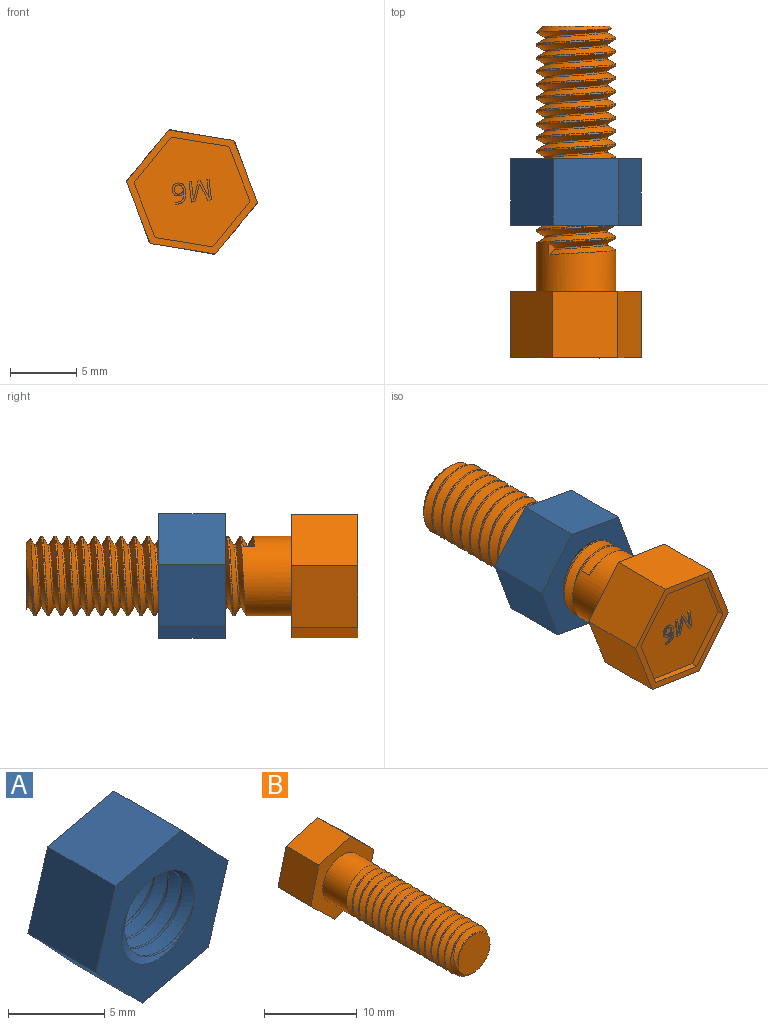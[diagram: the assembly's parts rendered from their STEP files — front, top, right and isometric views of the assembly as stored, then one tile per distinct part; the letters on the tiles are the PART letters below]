
ASSEMBLY  parts=2 mates=1
PART A: 12 faces, bbox 10.1x6.2x9.9 mm
  f0: plane 10.11x9.94mm, normal (0,-1,0), area 42.3mm2, adj f2,f3,f4,f5,f6,f7,f8,f9
  f1: plane 10.11x9.94mm, normal (0,1,0), area 42.3mm2, adj f2,f3,f4,f5,f6,f7,f8,f9
  f2: plane 5x4.78mm, normal (0.96,0,-0.29), area 25mm2, adj f0,f1,f3,f7
  f3: plane 5x3.65mm, normal (0.73,0,0.68), area 25mm2, adj f0,f1,f2,f4
  f4: plane 5x4.87mm, normal (-0.23,0,0.97), area 25mm2, adj f0,f1,f3,f5
  f5: plane 5x4.78mm, normal (-0.96,0,0.29), area 25mm2, adj f0,f1,f4,f6
  f6: plane 5x3.65mm, normal (-0.73,0,-0.68), area 25mm2, adj f0,f1,f5,f7
  f7: plane 5x4.87mm, normal (0.23,0,-0.97), area 25mm2, adj f0,f1,f2,f6
  f8: cylinder r=3mm len=6mm, axis (0,1,0), area 12.3mm2, adj f0,f1,f9,f11
  f9: bspline ~6.93x6mm, area 61.2mm2, adj f0,f1,f8,f10
  f10: cylinder r=2.37mm len=5mm, axis (0,1,0), area 11.6mm2, adj f0,f1,f9,f11
  f11: bspline ~6.93x6mm, area 61.2mm2, adj f0,f1,f8,f10
PART B: 84 faces, bbox 9.6x25.4x9.7 mm
  f0: plane 5x4.85mm, normal (0.97,0,-0.24), area 25mm2, adj f1,f5,f6,f7
  f1: plane 5x3.59mm, normal (0.7,0,0.72), area 25mm2, adj f0,f2,f6,f7
  f2: plane 5x4.81mm, normal (-0.27,0,0.96), area 25mm2, adj f1,f3,f6,f7
  f3: plane 5x4.85mm, normal (-0.97,0,0.24), area 25mm2, adj f2,f4,f6,f7
  f4: plane 5x3.59mm, normal (-0.7,0,-0.72), area 25mm2, adj f3,f5,f6,f7
  f5: plane 5x4.81mm, normal (0.27,0,-0.96), area 25mm2, adj f0,f4,f6,f7
  f6: plane 9.7x9.62mm, normal (0,-1,0), area 36.7mm2, adj f0,f1,f2,f3,f4,f5,f24
  f7: plane 9.7x9.62mm, normal (0,1,0), area 14.1mm2, adj f0,f1,f2,f3,f4,f5,f26,f27
  f8: cylinder r=3mm len=2.15mm, axis (0,1,0), area 0.1mm2, adj f9,f33,f35
  f9: cylinder r=3mm len=6mm, axis (0,1,0), area 2.4mm2, adj f8,f10,f35,f37
  f10: cylinder r=3mm len=6mm, axis (0,1,0), area 2.4mm2, adj f9,f11,f35,f37
  f11: cylinder r=3mm len=6mm, axis (0,1,0), area 2.4mm2, adj f10,f12,f35,f37
  f12: cylinder r=3mm len=6mm, axis (0,1,0), area 2.4mm2, adj f11,f13,f35,f37
  f13: cylinder r=3mm len=6mm, axis (0,1,0), area 2.4mm2, adj f12,f14,f35,f37
  f14: cylinder r=3mm len=6mm, axis (0,1,0), area 2.4mm2, adj f13,f15,f35,f37
  f15: cylinder r=3mm len=6mm, axis (0,1,0), area 2.4mm2, adj f14,f16,f35,f37
  f16: cylinder r=3mm len=6mm, axis (0,1,0), area 2.4mm2, adj f15,f17,f35,f37
  f17: cylinder r=3mm len=6mm, axis (0,1,0), area 2.4mm2, adj f16,f18,f35,f37
  f18: cylinder r=3mm len=6mm, axis (0,1,0), area 2.4mm2, adj f17,f19,f35,f37
  f19: cylinder r=3mm len=6mm, axis (0,1,0), area 2.4mm2, adj f18,f20,f35,f37
  f20: cylinder r=3mm len=6mm, axis (0,1,0), area 2.4mm2, adj f19,f21,f35,f37
  f21: cylinder r=3mm len=6mm, axis (0,1,0), area 2.4mm2, adj f20,f22,f35,f37
  f22: cylinder r=3mm len=6mm, axis (0,1,0), area 2.4mm2, adj f21,f23,f35,f37
  f23: cylinder r=3mm len=6mm, axis (0,1,0), area 2.4mm2, adj f22,f24,f35,f37
  f24: cylinder r=3mm len=6mm, axis (0,1,0), area 63.4mm2, adj f6,f23,f34,f35,f37
  f25: plane 5.01x4.88mm, normal (0,-1,0), area 19.2mm2, adj f33,f35,f36,f37
  f26: plane 3.17x3.08mm, normal (0.7,0,0.72), area 2.2mm2, adj f7,f27,f31,f32
  f27: plane 4.25x1.21mm, normal (-0.27,0,0.96), area 2.2mm2, adj f7,f26,f28,f32
  f28: plane 4.29x1.08mm, normal (-0.97,0,0.24), area 2.2mm2, adj f7,f27,f29,f32
  f29: plane 3.17x3.08mm, normal (-0.7,0,-0.72), area 2.2mm2, adj f7,f28,f30,f32
  f30: plane 4.25x1.21mm, normal (0.27,0,-0.96), area 2.2mm2, adj f7,f29,f31,f32
  f31: plane 4.29x1.08mm, normal (0.97,0,-0.24), area 2.2mm2, adj f7,f26,f30,f32
  f32: plane 8.58x8.51mm, normal (0,1,0), area 48.9mm2, adj f26,f27,f28,f29,f30,f31,f38,f39
  f33: cone r=2.5mm half-angle=45deg, axis (0,1,0), area 5mm2, adj f8,f25,f35,f37
  f34: plane 0.88x0.51mm, normal (0.81,0,-0.59), area 0.3mm2, adj f24,f35,f36,f37
  f35: bspline ~17.2x6.93mm, area 200.2mm2, adj f8,f9,f10,f11,f12,f13,f14,f15
  f36: cylinder r=2.37mm len=16.87mm, axis (0,1,0), area 56.6mm2, adj f25,f34,f35,f37
  f37: bspline ~17.53x6.93mm, area 206.3mm2, adj f9,f10,f11,f12,f13,f14,f15,f16
  f38: plane 0.14x0.1mm, normal (0,0,-1), area 0mm2, adj f32,f39,f55,f56
  f39: plane 1.35x0.52mm, normal (-0.93,0,-0.36), area 0.1mm2, adj f32,f38,f40,f56
  f40: plane 0.1x0.01mm, normal (0,0,-1), area 0mm2, adj f32,f39,f41,f56
  f41: extruded ~0.37x0.1mm, area 0mm2, adj f32,f40,f42,f56
  f42: plane 0.98x0.1mm, normal (1,0,0), area 0.1mm2, adj f32,f41,f43,f56
  f43: plane 0.18x0.1mm, normal (0,0,-1), area 0mm2, adj f32,f42,f44,f56
  f44: plane 1.53x0.1mm, normal (-1,0,0), area 0.2mm2, adj f32,f43,f45,f56
  f45: plane 0.27x0.1mm, normal (0,0,1), area 0mm2, adj f32,f44,f46,f56
  f46: plane 1.26x0.49mm, normal (0.93,0,0.36), area 0.1mm2, adj f32,f45,f47,f56
  f47: plane 0.1x0.01mm, normal (0,0,1), area 0mm2, adj f32,f46,f48,f56
  f48: plane 1.26x0.48mm, normal (-0.93,0,0.36), area 0.1mm2, adj f32,f47,f49,f56
  f49: plane 0.27x0.1mm, normal (0,0,1), area 0mm2, adj f32,f48,f50,f56
  f50: plane 1.53x0.1mm, normal (1,0,0), area 0.2mm2, adj f32,f49,f51,f56
  f51: plane 0.16x0.1mm, normal (0,0,-1), area 0mm2, adj f32,f50,f52,f56
  f52: plane 0.97x0.1mm, normal (-1,0,0), area 0.1mm2, adj f32,f51,f53,f56
  f53: extruded ~0.38x0.1mm, area 0mm2, adj f32,f52,f54,f56
  f54: plane 0.1x0.01mm, normal (0,0,-1), area 0mm2, adj f32,f53,f55,f56
  f55: plane 1.35x0.52mm, normal (0.93,0,-0.36), area 0.1mm2, adj f32,f38,f54,f56
  f56: plane 1.53x1.51mm, normal (0,1,0), area 1mm2, adj f38,f39,f40,f41,f42,f43,f44,f45
  f57: extruded ~0.5x0.14mm, area 0.1mm2, adj f32,f58,f81,f82
  f58: extruded ~0.38x0.18mm, area 0mm2, adj f32,f57,f59,f82
  f59: extruded ~0.35x0.14mm, area 0mm2, adj f32,f58,f60,f82
  f60: extruded ~0.38x0.13mm, area 0mm2, adj f32,f59,f61,f82
  f61: extruded ~0.34x0.12mm, area 0mm2, adj f32,f60,f62,f82
  f62: extruded ~0.32x0.12mm, area 0mm2, adj f32,f61,f63,f82
  f63: extruded ~0.36x0.18mm, area 0mm2, adj f32,f62,f64,f82
  f64: plane 0.1x0.01mm, normal (0,0,1), area 0mm2, adj f32,f63,f65,f82
  f65: extruded ~0.48x0.14mm, area 0.1mm2, adj f32,f64,f66,f82
  f66: extruded ~0.38x0.15mm, area 0mm2, adj f32,f65,f67,f82
  f67: extruded ~0.18x0.1mm, area 0mm2, adj f32,f66,f68,f82
  f68: plane 0.15x0.1mm, normal (-1,0,0), area 0mm2, adj f32,f67,f69,f82
  f69: extruded ~0.19x0.1mm, area 0mm2, adj f32,f68,f70,f82
  f70: extruded ~0.52x0.22mm, area 0.1mm2, adj f32,f69,f81,f82
  f71: extruded ~0.18x0.1mm, area 0mm2, adj f72,f80,f82,f83
  f72: extruded ~0.15x0.12mm, area 0mm2, adj f71,f73,f82,f83
  f73: extruded ~0.2x0.1mm, area 0mm2, adj f72,f74,f82,f83
  f74: extruded ~0.14x0.1mm, area 0mm2, adj f73,f75,f82,f83
  f75: extruded ~0.13x0.11mm, area 0mm2, adj f74,f76,f82,f83
  f76: extruded ~0.17x0.1mm, area 0mm2, adj f75,f77,f82,f83
  f77: extruded ~0.23x0.1mm, area 0mm2, adj f76,f78,f82,f83
  f78: extruded ~0.24x0.1mm, area 0mm2, adj f77,f79,f82,f83
  f79: extruded ~0.27x0.1mm, area 0mm2, adj f78,f80,f82,f83
  f80: extruded ~0.23x0.1mm, area 0mm2, adj f71,f79,f82,f83
  f81: extruded ~0.67x0.18mm, area 0.1mm2, adj f32,f57,f70,f82
  f82: plane 1.57x1mm, normal (0,1,0), area 0.6mm2, adj f57,f58,f59,f60,f61,f62,f63,f64
  f83: plane 0.69x0.65mm, normal (0,1,0), area 0.4mm2, adj f71,f72,f73,f74,f75,f76,f77,f78
PLACE A rot(axis=(0,1,0),83.2deg) t=(3.06,33.95,26.6)mm
PLACE B rot(axis=(1,0,0.06),180deg) t=(3.06,31.45,26.6)mm
MATE cylindrical B.f8 <-> A.f8  axis (0,-1,0) through (3.06,16.2,26.6)mm
